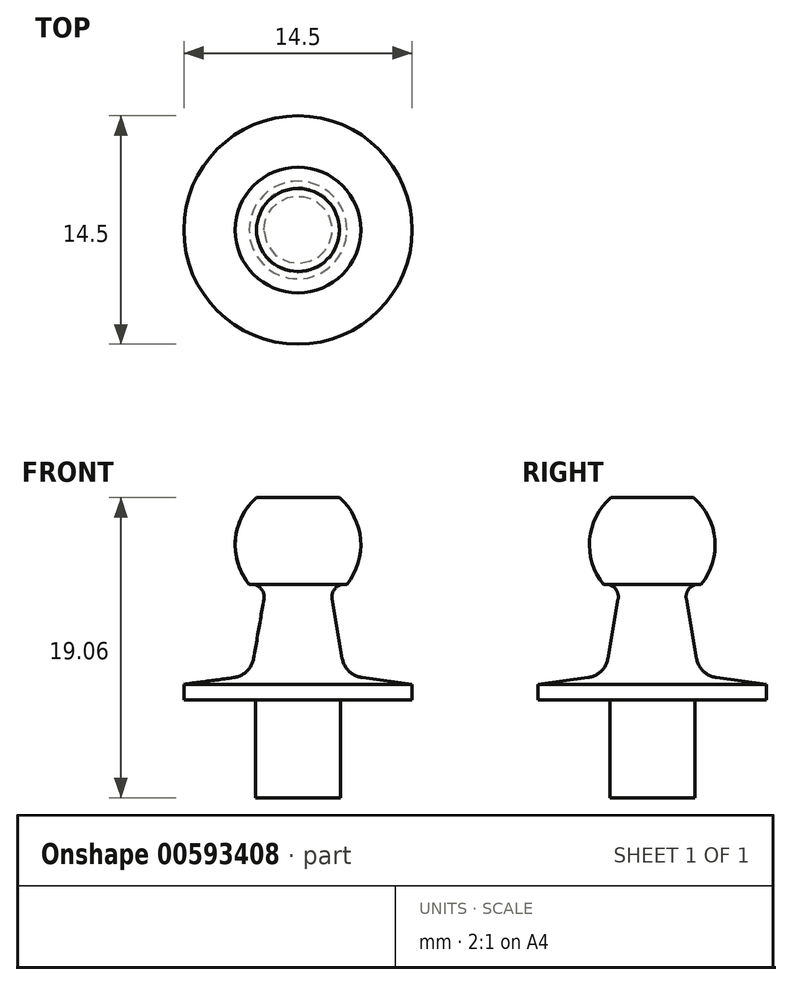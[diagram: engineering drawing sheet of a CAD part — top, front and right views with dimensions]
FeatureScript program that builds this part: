
annotation { "Feature Type Name" : "Feature", "Feature Type Description" : "" }
export const myFeature = defineFeature(function(context is Context, id is Id, definition is map)
    precondition{}
    {
        {
            var Q0;
            Q0=qCreatedBy(makeId("Front.planeOp"),FACE);
            var sketch = newSketch(context, id + "F0", { "sketchPlane" : qUnion([Q0])});
            skLineSegment(sketch, "E0", {"start": v(0, -16.7) * mm, "end": v(0, 20.47) * mm, "construction": true});
            skLineSegment(sketch, "E1", {"start": v(0, -6.2) * mm, "end": v(0, 12.86) * mm});
            skLineSegment(sketch, "E2", {"start": v(0, -6.2) * mm, "end": v(-2.7, -6.2) * mm});
            skLineSegment(sketch, "E3", {"start": v(-2.7, -6.2) * mm, "end": v(-2.7, 0) * mm});
            skLineSegment(sketch, "E4", {"start": v(-2.7, 0) * mm, "end": v(-7.25, 0) * mm});
            skLineSegment(sketch, "E5", {"start": v(-7.25, 0) * mm, "end": v(-7.25, 1) * mm});
            skLineSegment(sketch, "E6", {"start": v(-2.81, 2.65) * mm, "end": v(-2.16, 6.41) * mm});
            skLineSegment(sketch, "E7", {"start": v(-2.95, 7.35) * mm, "end": v(-3.1, 7.35) * mm});
            skLineSegment(sketch, "E8", {"start": v(-7.25, 1) * mm, "end": v(-4.1, 1.42) * mm});
            skLineSegment(sketch, "E9", {"start": v(0, 12.86) * mm, "end": v(-2.63, 12.86) * mm});
            skArc(sketch, "E10", {"start": v(-2.63, 12.86) * mm, "mid": v(-3.98, 10.2) * mm, "end": v(-3.1, 7.35) * mm});
            skPoint(sketch, "E11.visualSharp", {"position": v(-3, 1.57) * mm});
            skArc(sketch, "E11.filletArc", {"start": v(-4.1, 1.42) * mm, "mid": v(-3.25, 1.83) * mm, "end": v(-2.81, 2.65) * mm});
            skPoint(sketch, "E12.visualSharp", {"position": v(-2, 7.35) * mm});
            skArc(sketch, "E12.filletArc", {"start": v(-2.16, 6.41) * mm, "mid": v(-2.34, 7.07) * mm, "end": v(-2.95, 7.35) * mm});
            skSolve(sketch);
        }
        {
            var Q0;
            Q0=makeQuery(id+"F0.imprint","IMPRINT",FACE,{"disambiguationData":[TD([[makeQuery(id+"F0.imprint","IMPRINT",EDGE,{"derivedFrom":sQuery(id+"F0.wireOp",EDGE,"E1")}),1.0]])]});
            var Q1;
            Q1=sQuery(id+"F0.wireOp",EDGE,"E0");
            revolve(context, id + "F1", {"surfaceOperationType" : NewSurfaceOperationType.NEW, "entities" : qUnion([Q0]), "axis" : qUnion([Q1]), "revolveType" : RevolveType.FULL});
        }
    });
